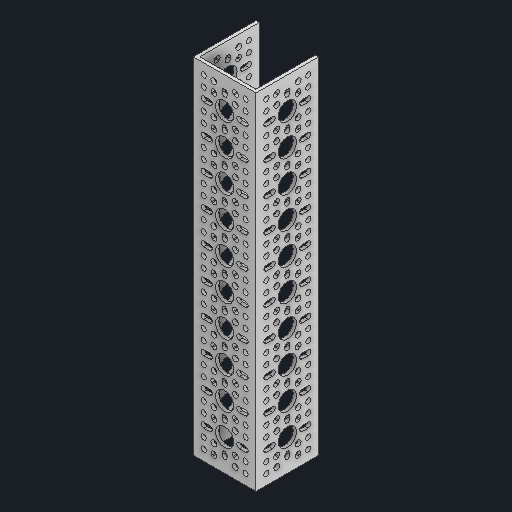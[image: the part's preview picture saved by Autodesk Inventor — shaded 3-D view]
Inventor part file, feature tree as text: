
AUTODESK INVENTOR PART (.ipt)
format: ipt  version: 2023 (Build 270158000, 158)  size: 1,131,520 bytes
history: native  units: in
note: dims shown in document units (in); Inventor stores cm internally (conversion verified against a paired STEP export)
features: mirror x1
ambient origin geometry x8: Origin, YZ Plane, XZ Plane, XY Plane, X Axis, Y Axis, Z Axis, Center Point
bodies: Solid1 (feature_tree)
feature tree (1):
  mirror  "Mirror5"
